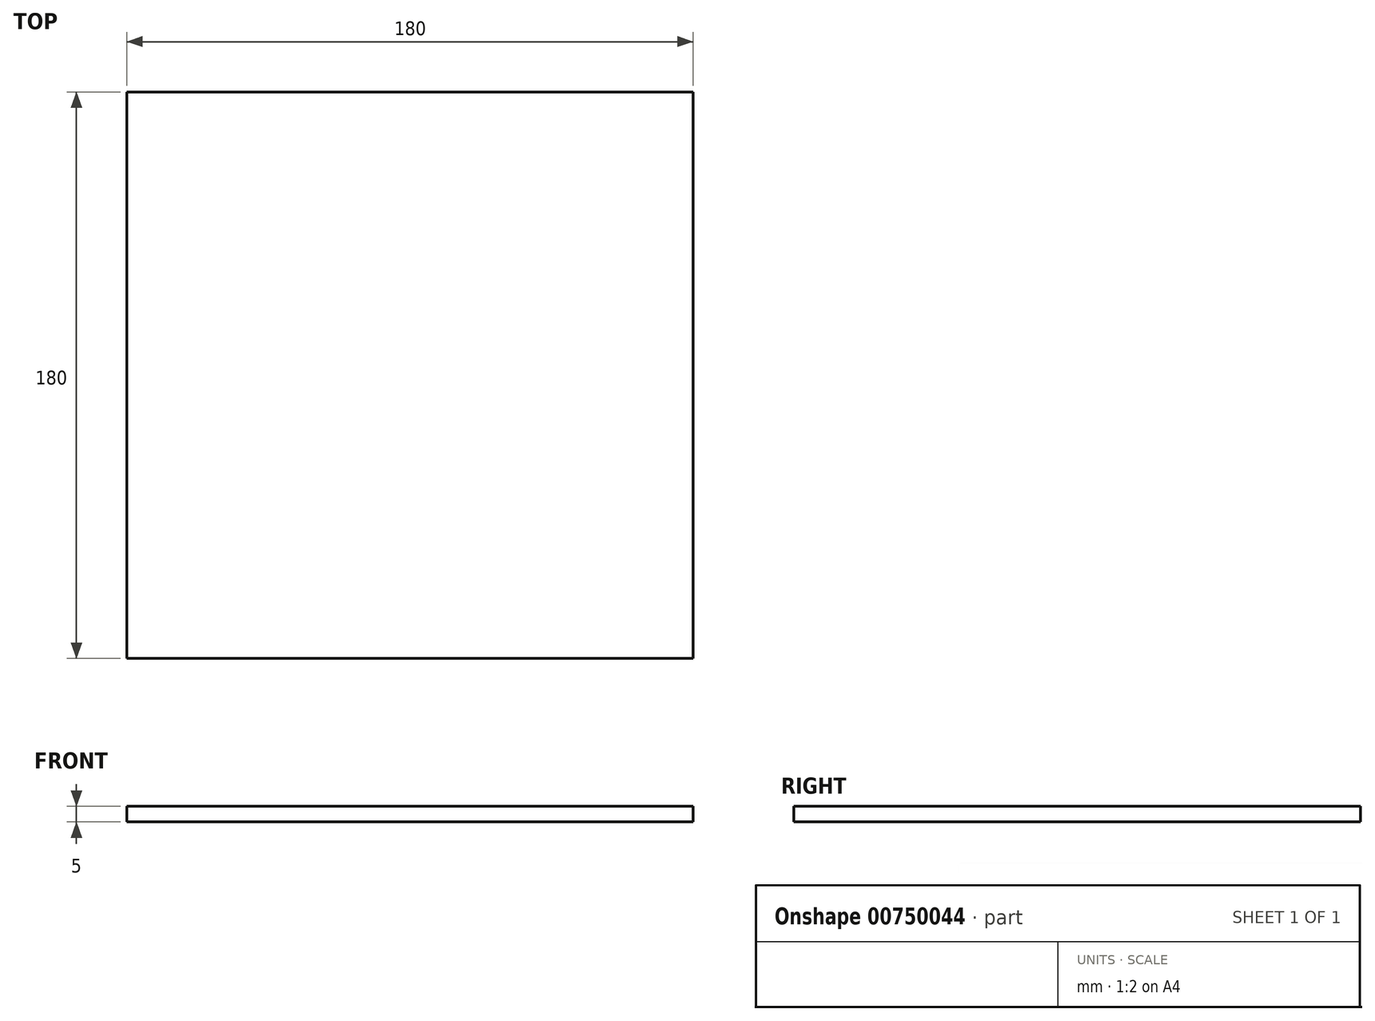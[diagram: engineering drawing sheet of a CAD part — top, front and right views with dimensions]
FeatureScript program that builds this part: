
annotation { "Feature Type Name" : "Feature", "Feature Type Description" : "" }
export const myFeature = defineFeature(function(context is Context, id is Id, definition is map)
    precondition{}
    {
        {
            var Q0;
            Q0=qCreatedBy(makeId("Top.planeOp"), FACE);
            var sketch = newSketch(context, id + "F0", { "sketchPlane" : qUnion([Q0])});
            skLineSegment(sketch, "E0.bottom", {"start": v(90, -90) * mm, "end": v(-90, -90) * mm});
            skLineSegment(sketch, "E0.top", {"start": v(90, 90) * mm, "end": v(-90, 90) * mm});
            skLineSegment(sketch, "E0.left", {"start": v(90, -90) * mm, "end": v(90, 90) * mm});
            skLineSegment(sketch, "E0.right", {"start": v(-90, -90) * mm, "end": v(-90, 90) * mm});
            skPoint(sketch, "E0.middle", {"position": v(0, 0) * mm});
            skSolve(sketch);
        }
        {
            var Q0;
            Q0 = qSketchRegion(id + "F0", true);
            extrude(context, id + "F1", {"entities" : qUnion([Q0]), "depth" : 5 * mm, "offsetDistance" : 25 * mm});
        }
    });
